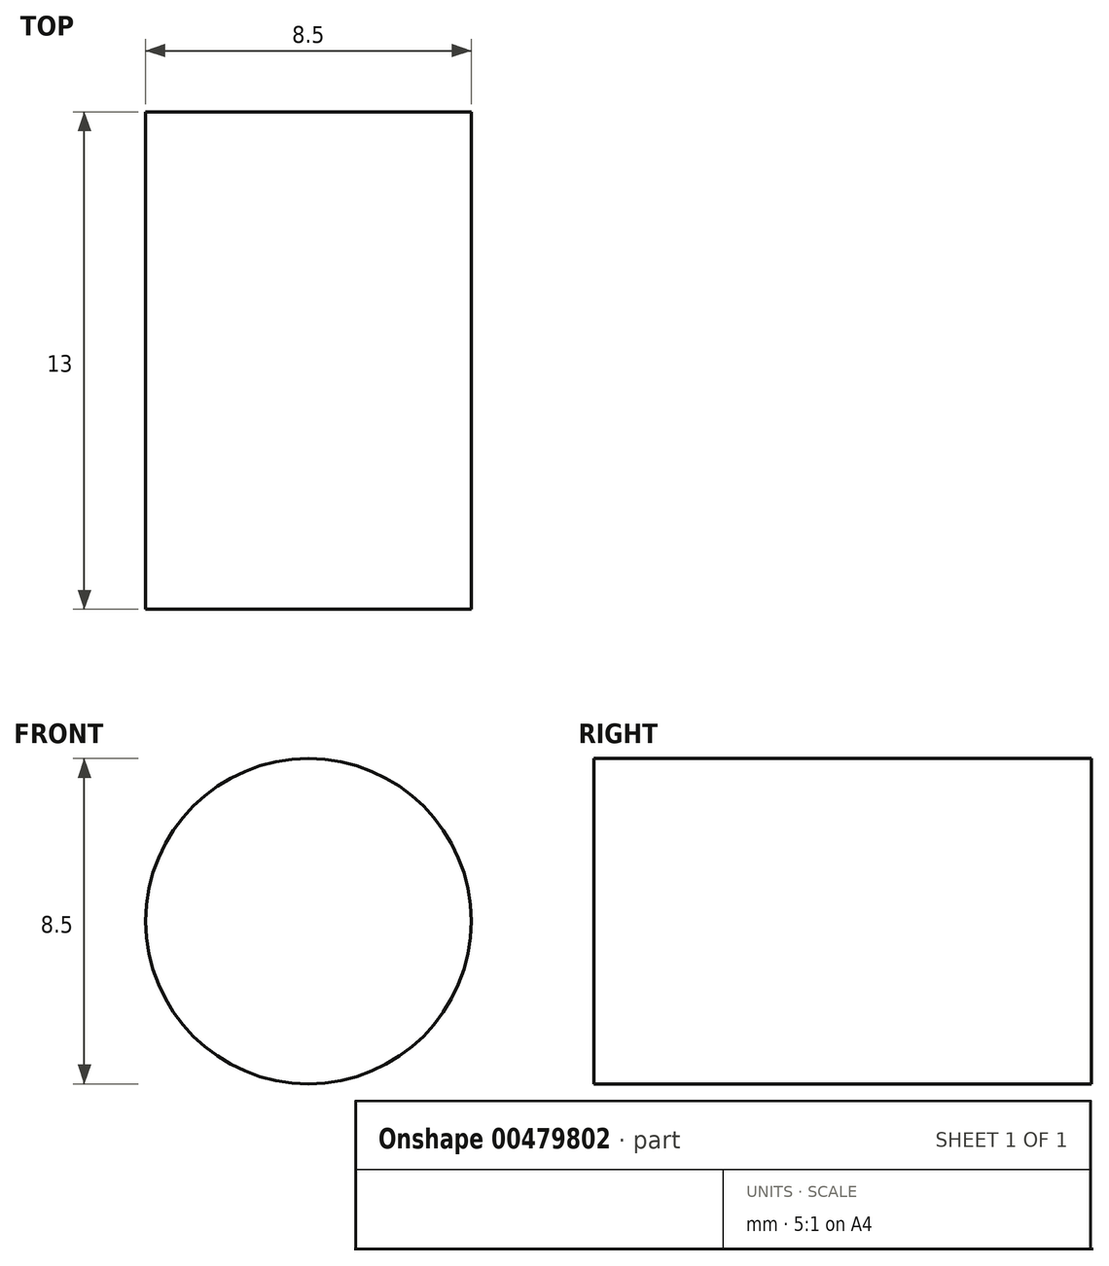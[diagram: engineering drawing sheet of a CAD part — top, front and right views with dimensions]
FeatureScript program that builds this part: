
annotation { "Feature Type Name" : "Feature", "Feature Type Description" : "" }
export const myFeature = defineFeature(function(context is Context, id is Id, definition is map)
    precondition{}
    {
        {
            var Q0;
            Q0=qCreatedBy(makeId("Front.planeOp"),FACE);
            var sketch = newSketch(context, id + "F0", { "sketchPlane" : qUnion([Q0])});
            skCircle(sketch, "E0", {"center": v(0, 0) * mm, "radius": 4.25 * mm});
            skSolve(sketch);
        }
        {
            var Q0;
            Q0=makeQuery(id+"F0.imprint","IMPRINT",FACE,{"disambiguationData":[TD([[makeQuery(id+"F0.imprint","IMPRINT",EDGE,{"derivedFrom":sQuery(id+"F0.wireOp",EDGE,"E0")}),1.0]])]});
            extrude(context, id + "F1", {"entities" : qUnion([Q0]), "depth" : 13 * mm});
        }
    });
